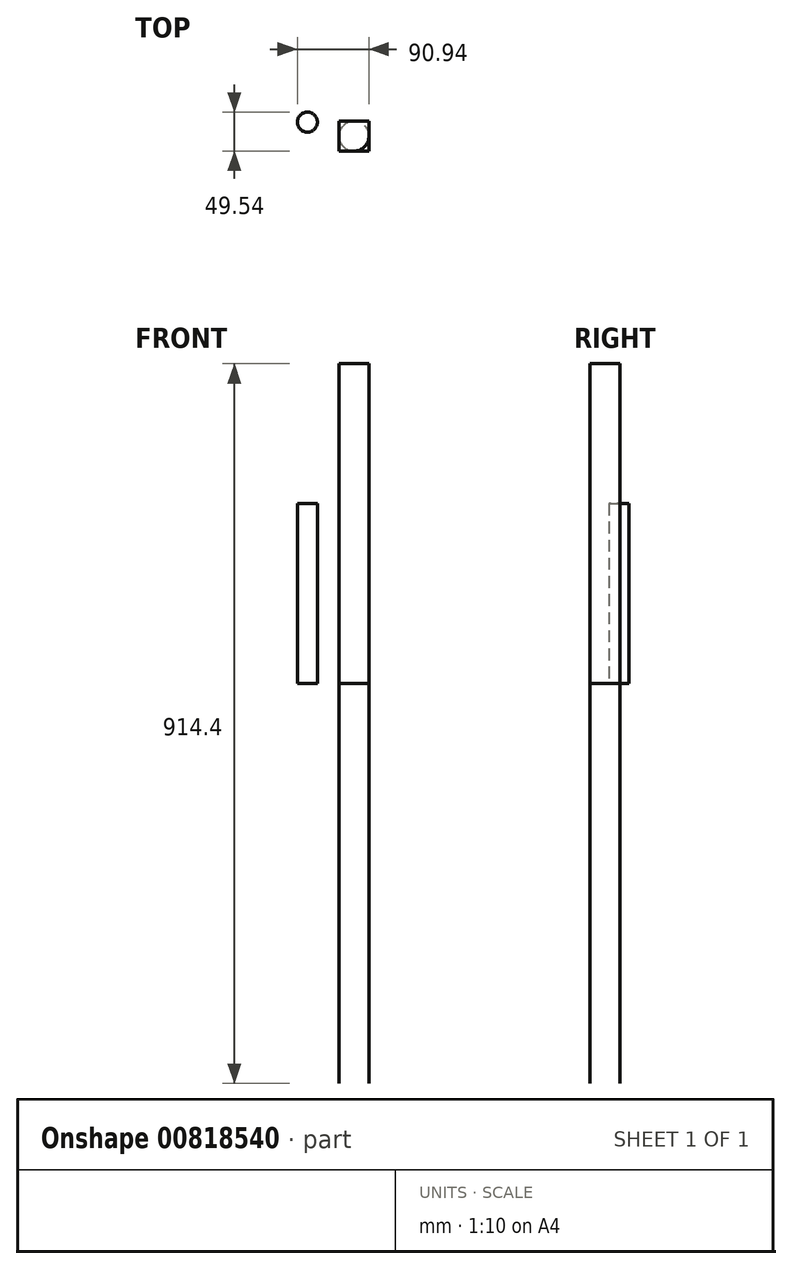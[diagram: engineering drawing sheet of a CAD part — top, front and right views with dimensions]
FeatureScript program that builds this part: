
annotation { "Feature Type Name" : "Feature", "Feature Type Description" : "" }
export const myFeature = defineFeature(function(context is Context, id is Id, definition is map)
    precondition{}
    {
        {
            var Q0;
            Q0=qCreatedBy(makeId("Top.planeOp"),FACE);
            var sketch = newSketch(context, id + "F0", { "sketchPlane" : qUnion([Q0])});
            skCircle(sketch, "E0", {"center": v(-59.2, 17.8) * mm, "radius": 12.7 * mm});
            skSolve(sketch);
        }
        {
            var Q0;
            Q0=makeQuery(id+"F0.imprint","IMPRINT",FACE,{"disambiguationData":[TD([[makeQuery(id+"F0.imprint","IMPRINT",EDGE,{"derivedFrom":sQuery(id+"F0.wireOp",EDGE,"E0")}),1.0]])]});
            extrude(context, id + "F1", {"entities" : qUnion([Q0]), "depth" : 228.6 * mm, "offsetDistance" : 25.4 * mm});
        }
        {
            var Q0;
            Q0=qCreatedBy(makeId("Right.planeOp"),FACE);
            var sketch = newSketch(context, id + "F2", { "sketchPlane" : qUnion([Q0])});
            skLineSegment(sketch, "E1.bottom", {"start": v(0, 0) * mm, "end": v(19.05, 0) * mm});
            skLineSegment(sketch, "E1.top", {"start": v(0, -508) * mm, "end": v(19.05, -508) * mm});
            skLineSegment(sketch, "E1.left", {"start": v(0, 0) * mm, "end": v(0, -508) * mm});
            skLineSegment(sketch, "E1.right", {"start": v(19.05, 0) * mm, "end": v(19.05, -508) * mm});
            skArc(sketch, "E2", {"start": v(0, -508) * mm, "mid": v(9.53, -517.52) * mm, "end": v(19.05, -508) * mm});
            skSolve(sketch);
        }
        {
            var Q0;
            Q0=makeQuery(id+"F2.imprint","IMPRINT",FACE,{"disambiguationData":[TD([[makeQuery(id+"F2.imprint","IMPRINT",EDGE,{"derivedFrom":sQuery(id+"F2.wireOp",EDGE,"E1.bottom")}),-1.0]])]});
            var Q1;
            Q1=makeQuery(id+"F2.imprint","IMPRINT",FACE,{"disambiguationData":[TD([[makeQuery(id+"F2.imprint","IMPRINT",EDGE,{"derivedFrom":sQuery(id+"F2.wireOp",EDGE,"E1.top")}),-1.0]])]});
            var Q2;
            Q2=sQuery(id+"F2.wireOp",EDGE,"E1.left");
            revolve(context, id + "F3", {"surfaceOperationType" : NewSurfaceOperationType.NEW, "entities" : qUnion([Q0, Q1]), "axis" : qUnion([Q2]), "revolveType" : RevolveType.FULL});
        }
        {
            var Q0;
            Q0=qCreatedBy(makeId("Top.planeOp"),FACE);
            var sketch = newSketch(context, id + "F4", { "sketchPlane" : qUnion([Q0])});
            skLineSegment(sketch, "E3.bottom", {"start": v(-19.05, 19.05) * mm, "end": v(19.05, 19.05) * mm});
            skLineSegment(sketch, "E3.top", {"start": v(-19.05, -19.05) * mm, "end": v(19.05, -19.05) * mm});
            skLineSegment(sketch, "E3.left", {"start": v(-19.05, 19.05) * mm, "end": v(-19.05, -19.05) * mm});
            skLineSegment(sketch, "E3.right", {"start": v(19.05, 19.05) * mm, "end": v(19.05, -19.05) * mm});
            skPoint(sketch, "E3.middle", {"position": v(0, 0) * mm});
            skSolve(sketch);
        }
        {
            var Q0;
            Q0=makeQuery(id+"F4.imprint","IMPRINT",FACE,{"disambiguationData":[TD([[makeQuery(id+"F4.imprint","IMPRINT",EDGE,{"derivedFrom":sQuery(id+"F4.wireOp",EDGE,"E3.bottom")}),-1.0]])]});
            extrude(context, id + "F5", {"entities" : qUnion([Q0]), "operationType" : NewBodyOperationType.ADD, "depth" : 406.4 * mm, "offsetDistance" : 25.4 * mm});
        }
    });
